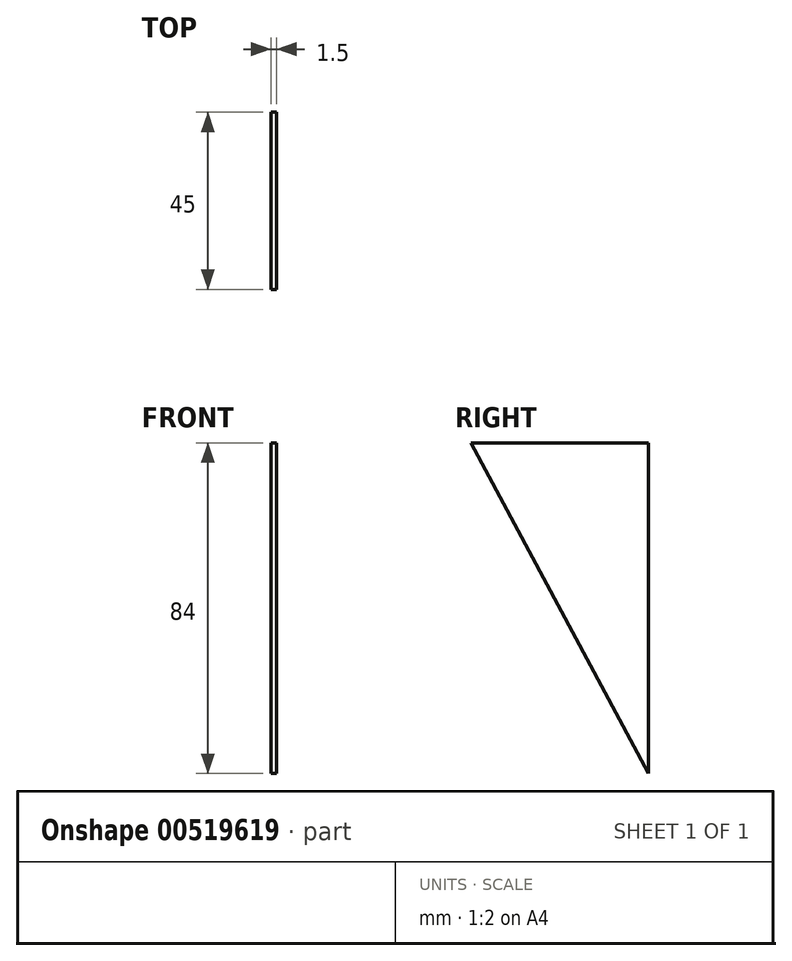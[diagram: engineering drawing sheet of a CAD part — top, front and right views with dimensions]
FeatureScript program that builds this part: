
annotation { "Feature Type Name" : "Feature", "Feature Type Description" : "" }
export const myFeature = defineFeature(function(context is Context, id is Id, definition is map)
    precondition{}
    {
        {
            var Q0;
            Q0=qCreatedBy(makeId("Right.planeOp"),FACE);
            var sketch = newSketch(context, id + "F0", { "sketchPlane" : qUnion([Q0])});
            skLineSegment(sketch, "E0", {"start": v(-23.88, 50.25) * mm, "end": v(21.12, -33.75) * mm});
            skLineSegment(sketch, "E1", {"start": v(21.12, -33.75) * mm, "end": v(21.12, 50.25) * mm});
            skLineSegment(sketch, "E2", {"start": v(21.12, 50.25) * mm, "end": v(-23.88, 50.25) * mm});
            skSolve(sketch);
        }
        {
            var Q0;
            Q0 = qSketchRegion(id + "F0", true);
            extrude(context, id + "F1", {"entities" : qUnion([Q0]), "depth" : 1.5 * mm, "offsetDistance" : 25 * mm});
        }
    });
